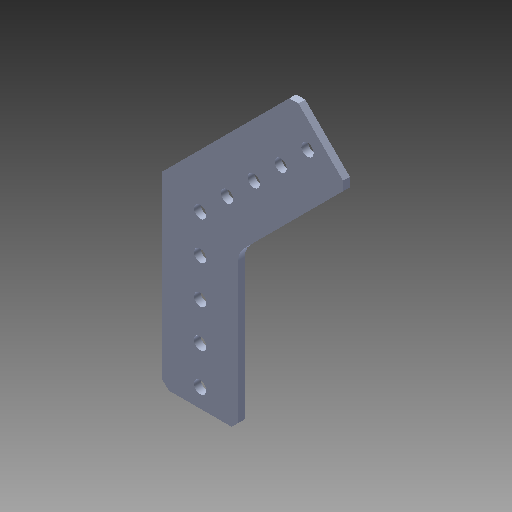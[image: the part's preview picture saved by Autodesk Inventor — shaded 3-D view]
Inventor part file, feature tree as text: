
AUTODESK INVENTOR PART (.ipt)
format: ipt  version: 2017 (Build 210142000, 142)  size: 119,296 bytes
history: native  units: in
note: dims shown in document units (in); Inventor stores cm internally (conversion verified against a paired STEP export)
features: fillet x1, other x1, imported_body x1
ambient origin geometry x8: Origin, YZ Plane, XZ Plane, XY Plane, X Axis, Y Axis, Z Axis, Center Point
bodies: Body1 (feature_tree)
feature tree (3):
  fillet  "Fillet2"  [1 undecoded]
  other  "VersaFrame 135 Degree Gusset1"
  imported_body  "Base1"
note: 1 required parameter value undecoded (feature->parameter linkage not recoverable at this tier; creation-order binding heuristic only, values carry confidence <= 0.55)
